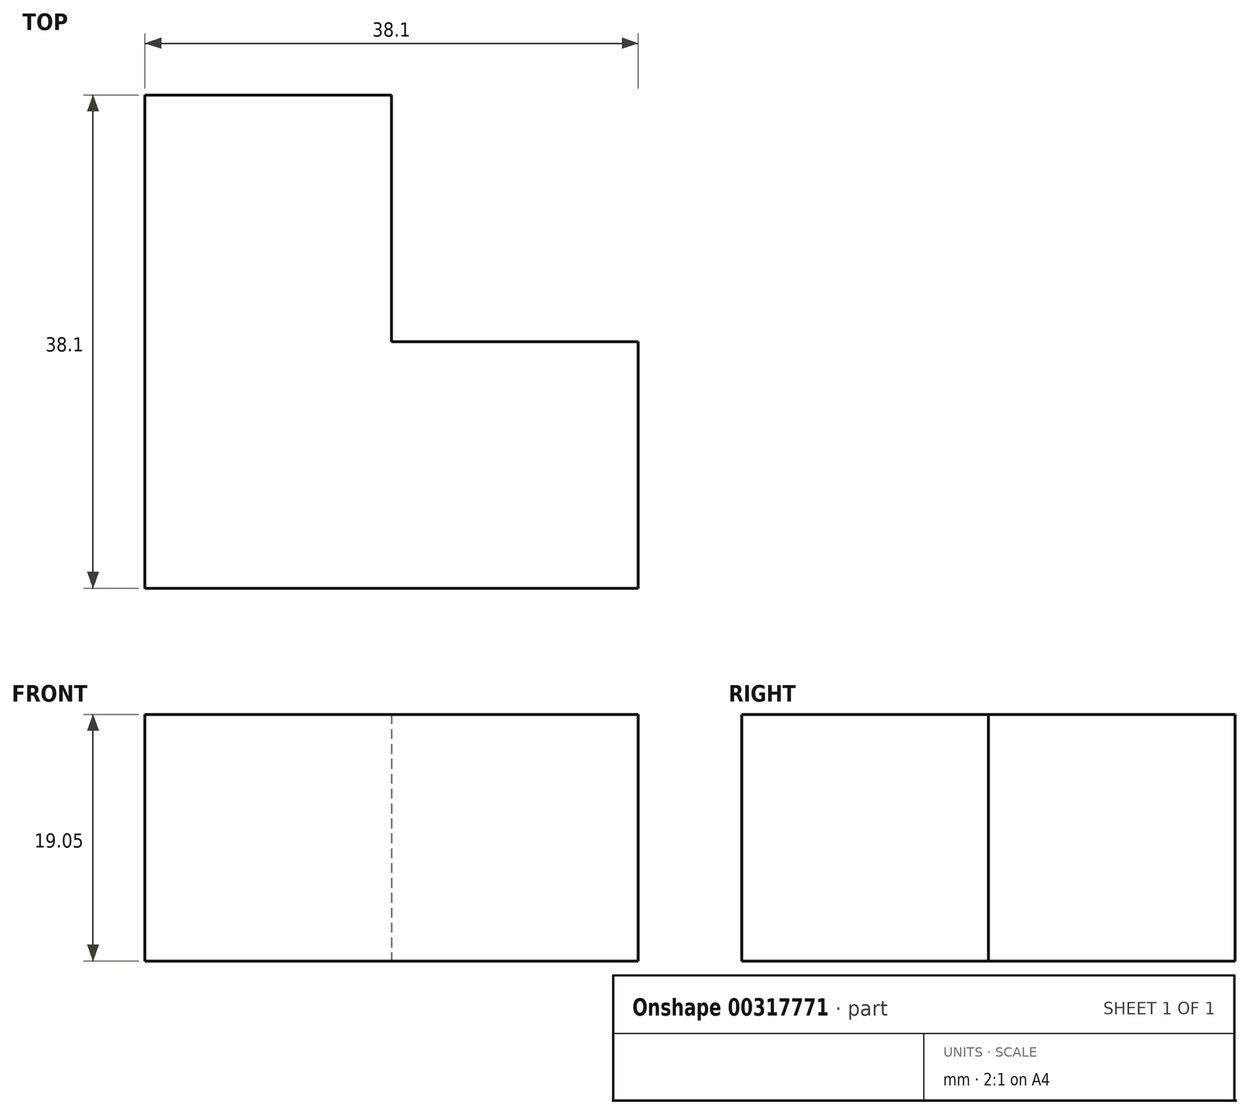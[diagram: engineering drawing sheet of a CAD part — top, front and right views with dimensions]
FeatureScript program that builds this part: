
annotation { "Feature Type Name" : "Feature", "Feature Type Description" : "" }
export const myFeature = defineFeature(function(context is Context, id is Id, definition is map)
    precondition{}
    {
        {
            var Q0;
            Q0=qCreatedBy(makeId("Top.planeOp"),FACE);
            var sketch = newSketch(context, id + "F0", { "sketchPlane" : qUnion([Q0])});
            skLineSegment(sketch, "E0.bottom", {"start": v(0, 0) * mm, "end": v(19.05, 0) * mm});
            skLineSegment(sketch, "E0.top", {"start": v(0, 38.1) * mm, "end": v(19.05, 38.1) * mm});
            skLineSegment(sketch, "E0.left", {"start": v(0, 0) * mm, "end": v(0, 38.1) * mm});
            skLineSegment(sketch, "E0.right", {"start": v(19.05, 19.05) * mm, "end": v(19.05, 38.1) * mm});
            skLineSegment(sketch, "E1.bottom", {"start": v(19.05, 0) * mm, "end": v(38.1, 0) * mm});
            skLineSegment(sketch, "E1.top", {"start": v(19.05, 19.05) * mm, "end": v(38.1, 19.05) * mm});
            skLineSegment(sketch, "E1.right", {"start": v(38.1, 0) * mm, "end": v(38.1, 19.05) * mm});
            skSolve(sketch);
        }
        {
            var Q0;
            Q0=makeQuery(id+"F0.imprint","IMPRINT",FACE,{"disambiguationData":[TD([[makeQuery(id+"F0.imprint","IMPRINT",EDGE,{"derivedFrom":sQuery(id+"F0.wireOp",EDGE,"E0.bottom")}),1.0]])]});
            extrude(context, id + "F1", {"entities" : qUnion([Q0]), "depth" : 19.05 * mm});
        }
    });
